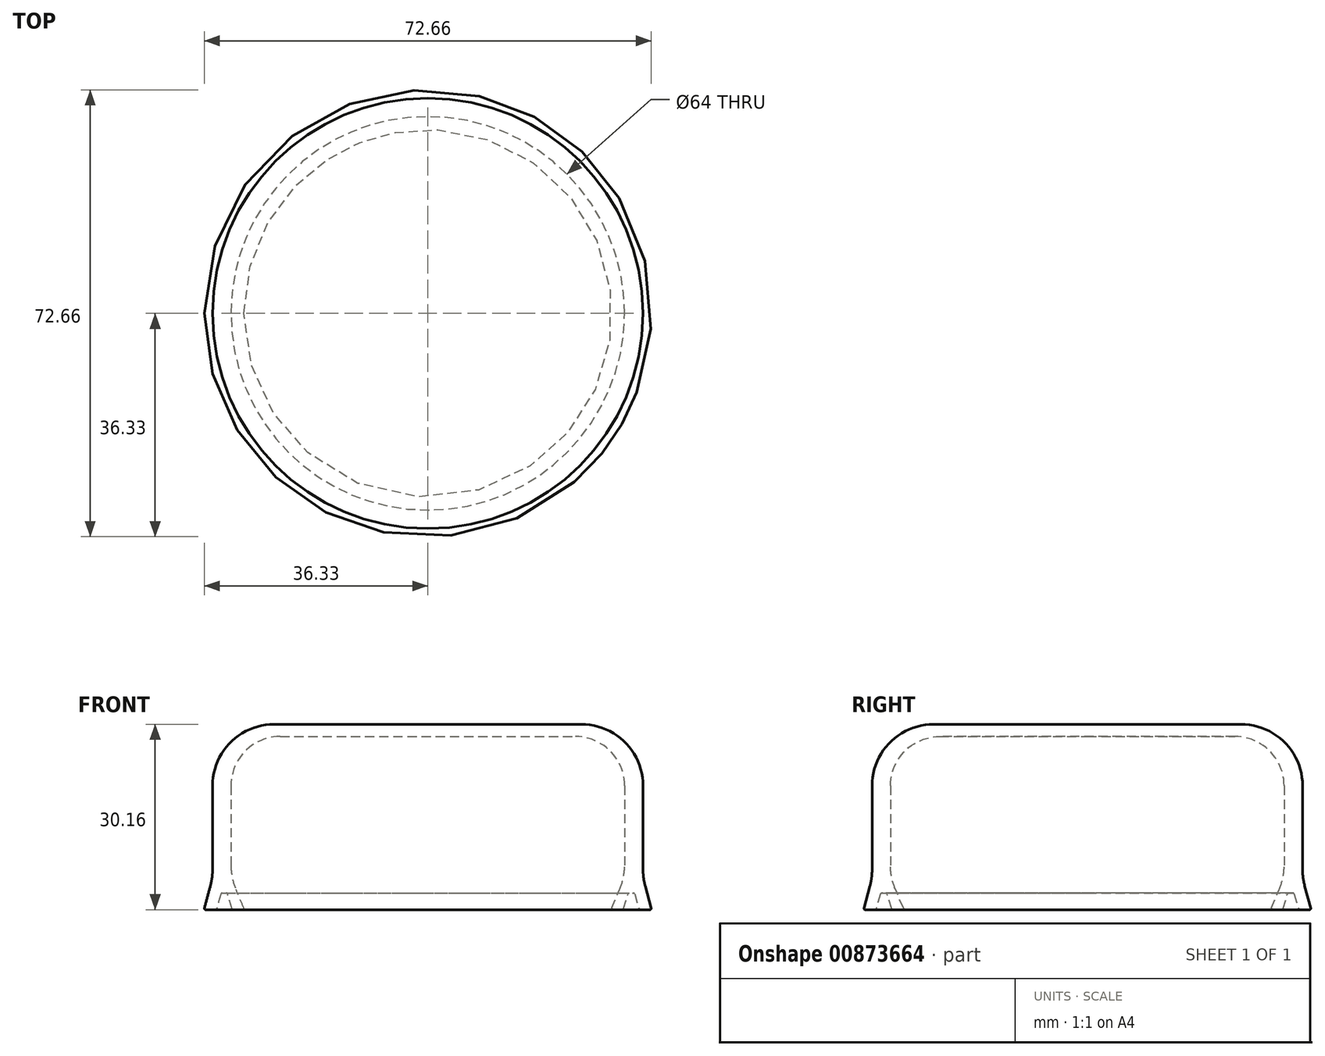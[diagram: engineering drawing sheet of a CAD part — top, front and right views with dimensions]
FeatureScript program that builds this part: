
annotation { "Feature Type Name" : "Feature", "Feature Type Description" : "" }
export const myFeature = defineFeature(function(context is Context, id is Id, definition is map)
    precondition{}
    {
        {
            var Q0;
            Q0=qCreatedBy(makeId("Front.planeOp"),FACE);
            var sketch = newSketch(context, id + "F0", { "sketchPlane" : qUnion([Q0])});
            skLineSegment(sketch, "E0", {"start": v(0, 28.16) * mm, "end": v(-24, 28.16) * mm});
            skLineSegment(sketch, "E1", {"start": v(-35, 6.48) * mm, "end": v(-35, 20.16) * mm});
            skLineSegment(sketch, "E2", {"start": v(-25, 30.16) * mm, "end": v(0, 30.16) * mm});
            skLineSegment(sketch, "E3", {"start": v(0, 30.16) * mm, "end": v(0, 28.16) * mm});
            skLineSegment(sketch, "E4", {"start": v(-34.54, 0) * mm, "end": v(-36.13, 0) * mm});
            skLineSegment(sketch, "E5", {"start": v(-36.32, 0.25) * mm, "end": v(-35.34, 3.88) * mm});
            skLineSegment(sketch, "E6", {"start": v(-31.64, 0) * mm, "end": v(-30.1, 0) * mm});
            skLineSegment(sketch, "E7", {"start": v(-29.9, 0.28) * mm, "end": v(-31.2, 3.27) * mm});
            skPoint(sketch, "E8.visualSharp", {"position": v(-35, 5.16) * mm});
            skArc(sketch, "E8.filletArc", {"start": v(-35.34, 3.88) * mm, "mid": v(-35.09, 5.17) * mm, "end": v(-35, 6.48) * mm});
            skLineSegment(sketch, "E9", {"start": v(-32, 20.16) * mm, "end": v(-32, 7.2) * mm});
            skPoint(sketch, "E10.visualSharp", {"position": v(-32, 5.16) * mm});
            skArc(sketch, "E10.filletArc", {"start": v(-32, 7.2) * mm, "mid": v(-31.8, 5.2) * mm, "end": v(-31.2, 3.27) * mm});
            skPoint(sketch, "E11.visualSharp", {"position": v(-35, 30.16) * mm});
            skArc(sketch, "E11.filletArc", {"start": v(-25, 30.16) * mm, "mid": v(-32.07, 27.23) * mm, "end": v(-35, 20.16) * mm});
            skPoint(sketch, "E12.visualSharp", {"position": v(-32, 28.16) * mm});
            skArc(sketch, "E12.filletArc", {"start": v(-24, 28.16) * mm, "mid": v(-29.66, 25.81) * mm, "end": v(-32, 20.16) * mm});
            skLineSegment(sketch, "E13", {"start": v(-34.35, 0.14) * mm, "end": v(-33.63, 2.56) * mm});
            skLineSegment(sketch, "E14", {"start": v(-33.44, 2.7) * mm, "end": v(-32.74, 2.7) * mm});
            skLineSegment(sketch, "E15", {"start": v(-32.55, 2.56) * mm, "end": v(-31.83, 0.14) * mm});
            skPoint(sketch, "E16.visualSharp", {"position": v(-33.59, 2.7) * mm});
            skArc(sketch, "E16.filletArc", {"start": v(-33.44, 2.7) * mm, "mid": v(-33.56, 2.67) * mm, "end": v(-33.63, 2.56) * mm});
            skPoint(sketch, "E17.visualSharp", {"position": v(-32.59, 2.7) * mm});
            skArc(sketch, "E17.filletArc", {"start": v(-32.55, 2.56) * mm, "mid": v(-32.62, 2.67) * mm, "end": v(-32.74, 2.7) * mm});
            skPoint(sketch, "E18.visualSharp", {"position": v(-36.39, 0) * mm});
            skArc(sketch, "E18.filletArc", {"start": v(-36.32, 0.25) * mm, "mid": v(-36.29, 0.08) * mm, "end": v(-36.13, 0) * mm});
            skPoint(sketch, "E19.visualSharp", {"position": v(-34.39, 0) * mm});
            skArc(sketch, "E19.filletArc", {"start": v(-34.54, 0) * mm, "mid": v(-34.42, 0.04) * mm, "end": v(-34.35, 0.14) * mm});
            skPoint(sketch, "E20.visualSharp", {"position": v(-31.79, 0) * mm});
            skArc(sketch, "E20.filletArc", {"start": v(-31.83, 0.14) * mm, "mid": v(-31.76, 0.04) * mm, "end": v(-31.64, 0) * mm});
            skPoint(sketch, "E21.visualSharp", {"position": v(-29.79, 0) * mm});
            skArc(sketch, "E21.filletArc", {"start": v(-30.1, 0) * mm, "mid": v(-29.93, 0.09) * mm, "end": v(-29.9, 0.28) * mm});
            skSolve(sketch);
        }
        {
            var Q0;
            Q0=qCreatedBy(makeId("Front.planeOp"),FACE);
            var sketch = newSketch(context, id + "F1", { "sketchPlane" : qUnion([Q0])});
            skLineSegment(sketch, "E22", {"start": v(0, 0) * mm, "end": v(0, 36.2) * mm, "construction": true});
            skSolve(sketch);
        }
        {
            var Q0;
            Q0 = qSketchRegion(id + "F0", true);
            var Q1;
            Q1=sQuery(id+"F1.wireOp",EDGE,"E22");
            revolve(context, id + "F2", {"surfaceOperationType" : NewSurfaceOperationType.NEW, "entities" : qUnion([Q0]), "axis" : qUnion([Q1]), "revolveType" : RevolveType.FULL});
        }
    });
